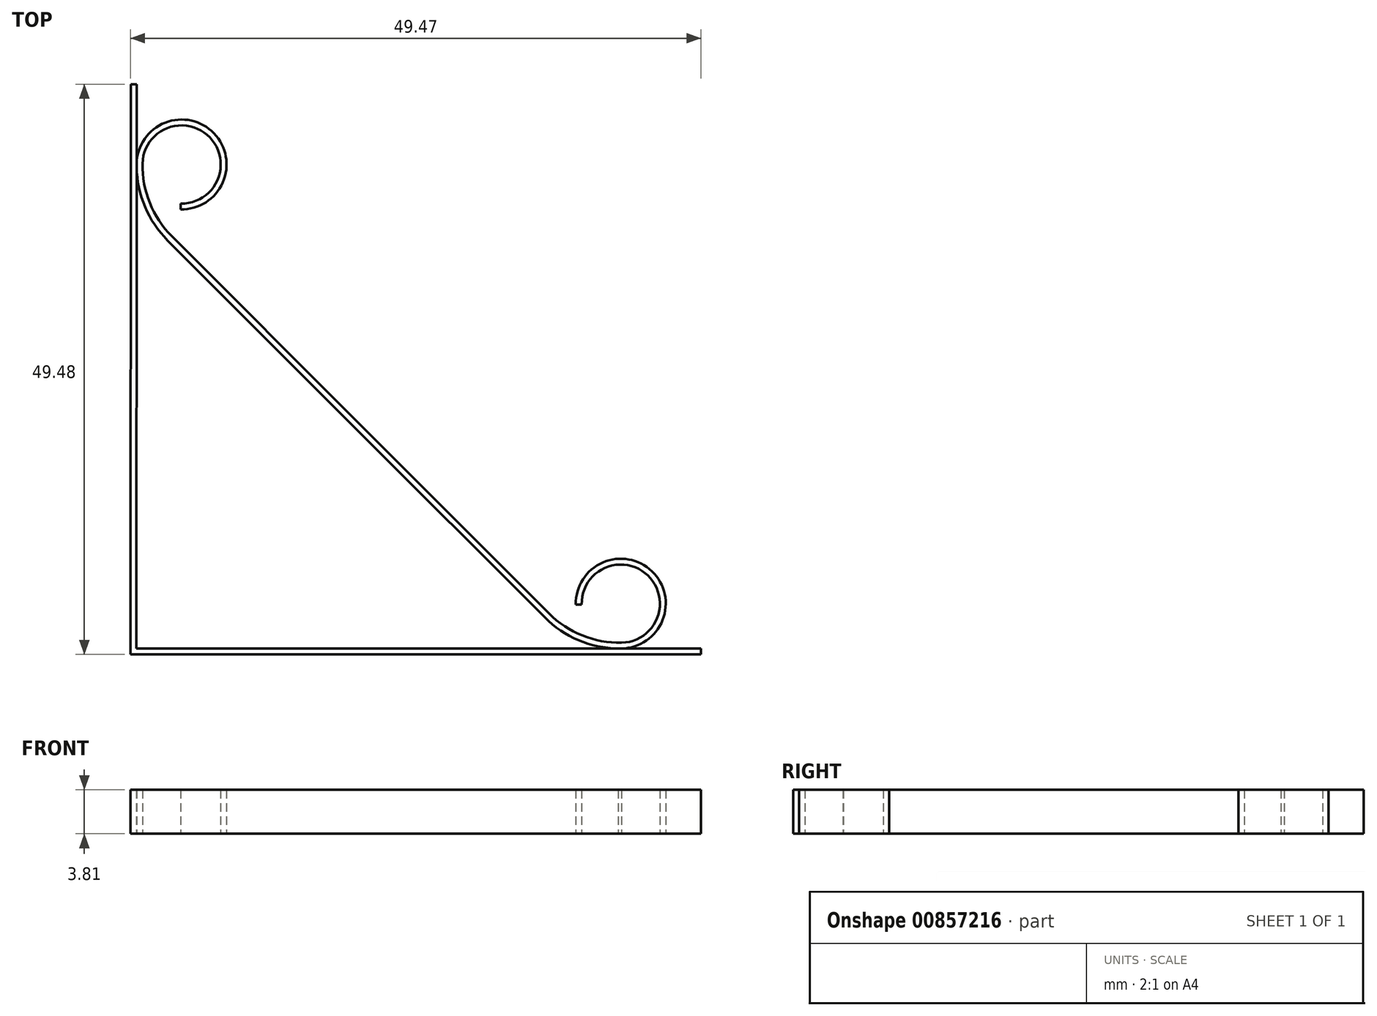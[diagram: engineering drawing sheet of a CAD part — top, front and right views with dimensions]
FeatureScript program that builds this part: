
annotation { "Feature Type Name" : "Feature", "Feature Type Description" : "" }
export const myFeature = defineFeature(function(context is Context, id is Id, definition is map)
    precondition{}
    {
        {
            var Q0;
            Q0=qCreatedBy(makeId("Top.planeOp"),FACE);
            var sketch = newSketch(context, id + "F0", { "sketchPlane" : qUnion([Q0])});
            skLineSegment(sketch, "E0", {"start": v(-2.2, 3.93) * mm, "end": v(14.16, -12.43) * mm});
            skPoint(sketch, "E1", {"position": v(-2.2, 3.94) * mm});
            skArc(sketch, "E2", {"start": v(14.16, -12.43) * mm, "mid": v(17.2, -14.45) * mm, "end": v(20.8, -15.12) * mm});
            skArc(sketch, "E3", {"start": v(20.8, -15.12) * mm, "mid": v(23.45, -8.41) * mm, "end": v(16.85, -11.3) * mm});
            skLineSegment(sketch, "E4", {"start": v(27.7, -15.12) * mm, "end": v(-21.27, -15.12) * mm});
            skLineSegment(sketch, "E5", {"start": v(-1.84, 4.29) * mm, "end": v(-21.27, -15.12) * mm});
            skLineSegment(sketch, "E6.MirrorCS", {"start": v(-21.23, 33.85) * mm, "end": v(-21.27, -15.12) * mm});
            skLineSegment(sketch, "E7.0", {"start": v(-21.74, 33.85) * mm, "end": v(-21.77, -15.63) * mm});
            skLineSegment(sketch, "E8.0", {"start": v(27.7, -15.63) * mm, "end": v(-21.77, -15.63) * mm});
            skLineSegment(sketch, "E9", {"start": v(27.7, -15.12) * mm, "end": v(27.7, -15.63) * mm});
            skLineSegment(sketch, "E10", {"start": v(-21.74, 33.85) * mm, "end": v(-21.23, 33.85) * mm});
            skArc(sketch, "E11.0", {"start": v(14.52, -12.07) * mm, "mid": v(17.4, -13.98) * mm, "end": v(20.82, -14.61) * mm});
            skArc(sketch, "E12.0", {"start": v(20.82, -14.61) * mm, "mid": v(23.1, -8.77) * mm, "end": v(17.35, -11.29) * mm});
            skLineSegment(sketch, "E13", {"start": v(16.85, -11.3) * mm, "end": v(17.35, -11.29) * mm});
            skLineSegment(sketch, "E14.trimOffspring", {"start": v(-1.84, 4.29) * mm, "end": v(14.52, -12.07) * mm});
            skLineSegment(sketch, "E15.MirrorCS", {"start": v(27.7, -15.63) * mm, "end": v(27.7, -15.12) * mm});
            skLineSegment(sketch, "E16.MirrorCS", {"start": v(-17.42, 23) * mm, "end": v(-17.4, 23.5) * mm});
            skArc(sketch, "E17.MirrorCS", {"start": v(-20.73, 26.96) * mm, "mid": v(-14.89, 29.24) * mm, "end": v(-17.4, 23.5) * mm});
            skLineSegment(sketch, "E18.MirrorCS", {"start": v(-1.84, 4.29) * mm, "end": v(-18.19, 20.66) * mm});
            skArc(sketch, "E19.MirrorCS", {"start": v(-21.24, 26.95) * mm, "mid": v(-14.53, 29.6) * mm, "end": v(-17.42, 23) * mm});
            skArc(sketch, "E20.MirrorCS", {"start": v(-18.55, 20.3) * mm, "mid": v(-20.57, 23.36) * mm, "end": v(-21.24, 26.95) * mm});
            skLineSegment(sketch, "E21.MirrorCS", {"start": v(-2.2, 3.93) * mm, "end": v(-18.55, 20.3) * mm});
            skArc(sketch, "E22.MirrorCS", {"start": v(-18.19, 20.66) * mm, "mid": v(-20.1, 23.55) * mm, "end": v(-20.73, 26.96) * mm});
            skSolve(sketch);
        }
        {
            var Q0;
            Q0=makeQuery(id+"F0.imprint","IMPRINT",FACE,{"disambiguationData":[TD([[makeQuery(id+"F0.imprint","IMPRINT",EDGE,{"derivedFrom":sQuery(id+"F0.wireOp",EDGE,"E7.0")}),1.0]])]});
            var Q1;
            Q1=makeQuery(id+"F0.imprint","IMPRINT",FACE,{"disambiguationData":[TD([[makeQuery(id+"F0.imprint","IMPRINT",EDGE,{"derivedFrom":sQuery(id+"F0.wireOp",EDGE,"E16.MirrorCS")}),-1.0]])]});
            var Q2;
            {var subQ1=sQuery(id+"F0.wireOp",EDGE,"E0");Q2=makeQuery(id+"F0.imprint","IMPRINT",FACE,{"disambiguationData":[TD([[makeQuery(id+"F0.imprint","IMPRINT",EDGE,{"derivedFrom":subQ1}),1.0]])]});}
            extrude(context, id + "F1", {"entities" : qUnion([Q0, Q1, Q2]), "depth" : 3.8 * mm, "offsetDistance" : 25.4 * mm});
        }
    });
